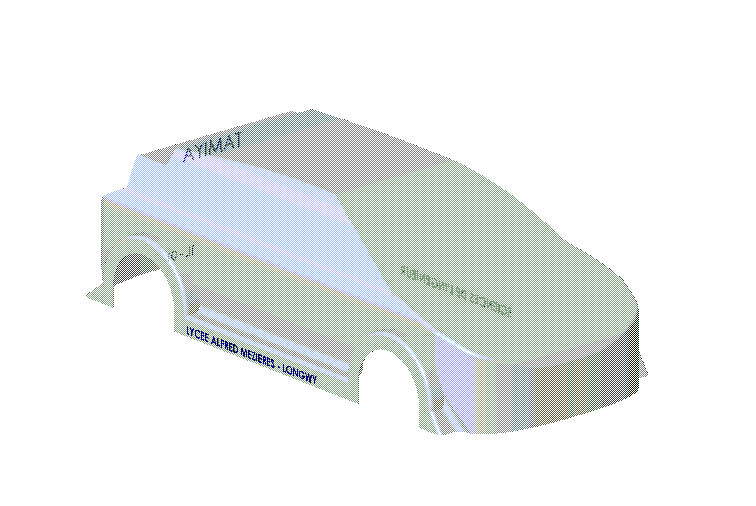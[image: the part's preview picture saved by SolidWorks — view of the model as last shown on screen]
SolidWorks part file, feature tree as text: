
SOLIDWORKS PART (.sldprt)
format: sldprt  version: not decoded by parser v0  size: 1,187,840 bytes
history: native  units: mm
features: sketch x7, plane x4, extrude x4, cut_extrude x3, fillet x3, material x1, shell x1 (+8 scaffold rows collapsed)
feature tree (31):
  scaffold x8  (default folders/planes/origin — collapsed)
  material  "Matériau <non spécifié>"
  plane  "Plane1"
  plane  "Plane2"
  plane  "Plane3"
  sketch  "Esquisse1"  dims[c1.D3=68.0mm c1.D4=68.0mm c1.D5=10.0mm c1.D1=180.0mm c1.D2=18.0mm c1.D6=125.0mm c1.D7=80.0mm c2.D6=8.0mm c2.D7=255.0mm c2.D1=420.0mm c2.D2=330.0mm c2.D3=124.0mm c2.D4=255.0mm]
  extrude  "Base-Extrusion"  Depth=170mm
  sketch  "Esquisse2"  dims[D1=68.0mm]
  cut_extrude  "Enlèv. mat.-Extru.2"  Depth=170mm
  sketch  "Esquisse5"
  cut_extrude  "Enlèv. mat.-Extru.4"  Depth=660mm
  sketch  "Esquisse6"  dims[D4=65.0mm D5=65.0mm D6=90.0mm D7=90.0mm D1=15.0mm D2=85.0mm D3=260.0mm]
  extrude  "Boss.-Extru.3"  Depth=190mm
  fillet  "Congé1"  Radius=3mm
  fillet  "Congé2"  Radius=2mm
  fillet  "Congé3"  Radius=5mm
  sketch  "Esquisse8"  dims[c1.D4=65.0mm c1.D5=65.0mm c1.D6=100.0mm c1.D7=100.0mm c1.D1=65.0mm c1.D2=65.0mm c2.D1=65.0mm c2.D2=65.0mm c3.D1=15.0mm c3.D2=90.0mm c3.D3=260.0mm c4.D2=32.0mm c4.D4=85.0mm]
  shell  "Coque1"  Thickness=1mm
  cut_extrude  "Enlèv. mat.-Extru.6"  Depth=660mm
  plane  "Plan1"  Offset=270mm
  sketch  "Esquisse11"  dims[D1=12.0mm]
  extrude  "Boss.-Extru.4"  Depth=0.5mm
  sketch  "Esquisse14"  dims[D1=45.0mm D2=15.0mm]
  extrude  "Boss.-Extru.5"  Depth=1mm
decode coverage: 17 of 18 modeling features carry decoded parameters
note: suppression state not decoded; provenance and decode notes live in map.json
